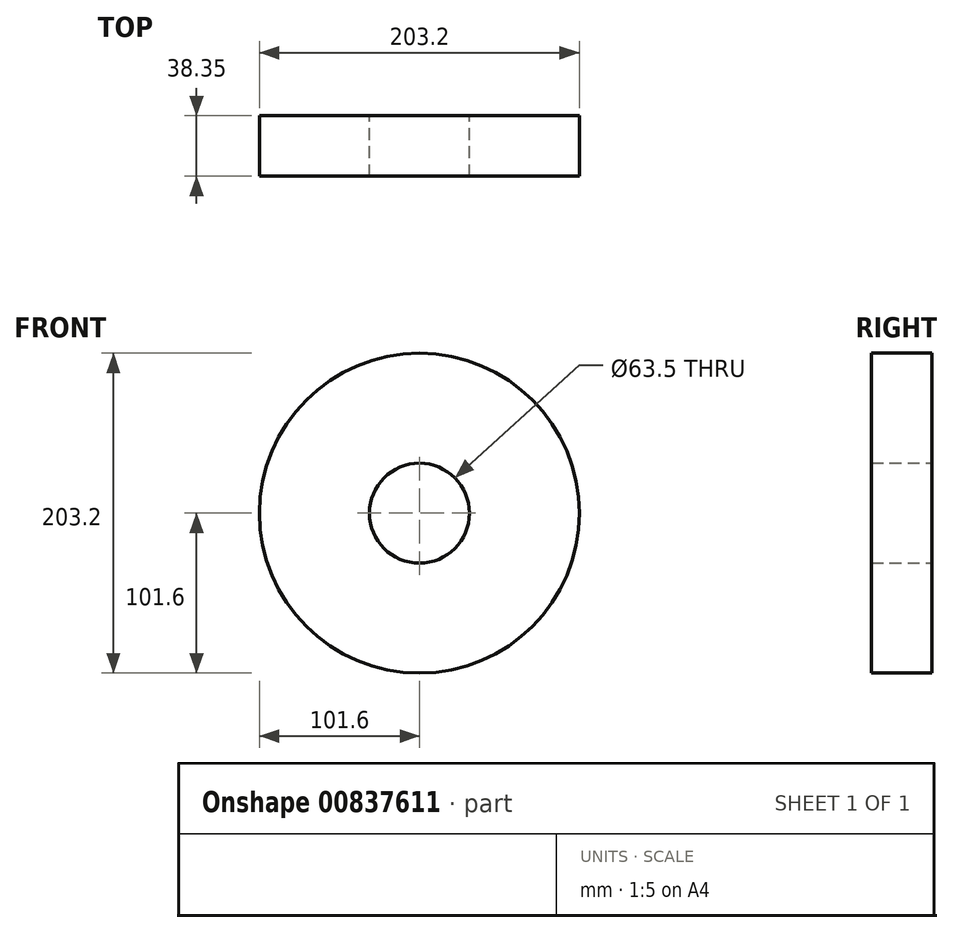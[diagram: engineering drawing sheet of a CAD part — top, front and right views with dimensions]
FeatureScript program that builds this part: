
annotation { "Feature Type Name" : "Feature", "Feature Type Description" : "" }
export const myFeature = defineFeature(function(context is Context, id is Id, definition is map)
    precondition{}
    {
        {
            var Q0;
            Q0=qCreatedBy(makeId("Front.planeOp"),FACE);
            var sketch = newSketch(context, id + "F0", { "sketchPlane" : qUnion([Q0])});
            skCircle(sketch, "E0", {"center": v(0, 0) * mm, "radius": 101.6 * mm});
            skCircle(sketch, "E1", {"center": v(0, 0) * mm, "radius": 31.75 * mm});
            skSolve(sketch);
        }
        {
            var Q0;
            Q0=makeQuery(id+"F0.imprint","IMPRINT",FACE,{"disambiguationData":[TD([[makeQuery(id+"F0.imprint","IMPRINT",EDGE,{"derivedFrom":sQuery(id+"F0.wireOp",EDGE,"E0")}),1.0]])]});
            extrude(context, id + "F1", {"entities" : qUnion([Q0]), "depth" : 38.35 * mm, "offsetDistance" : 25.4 * mm});
        }
    });
